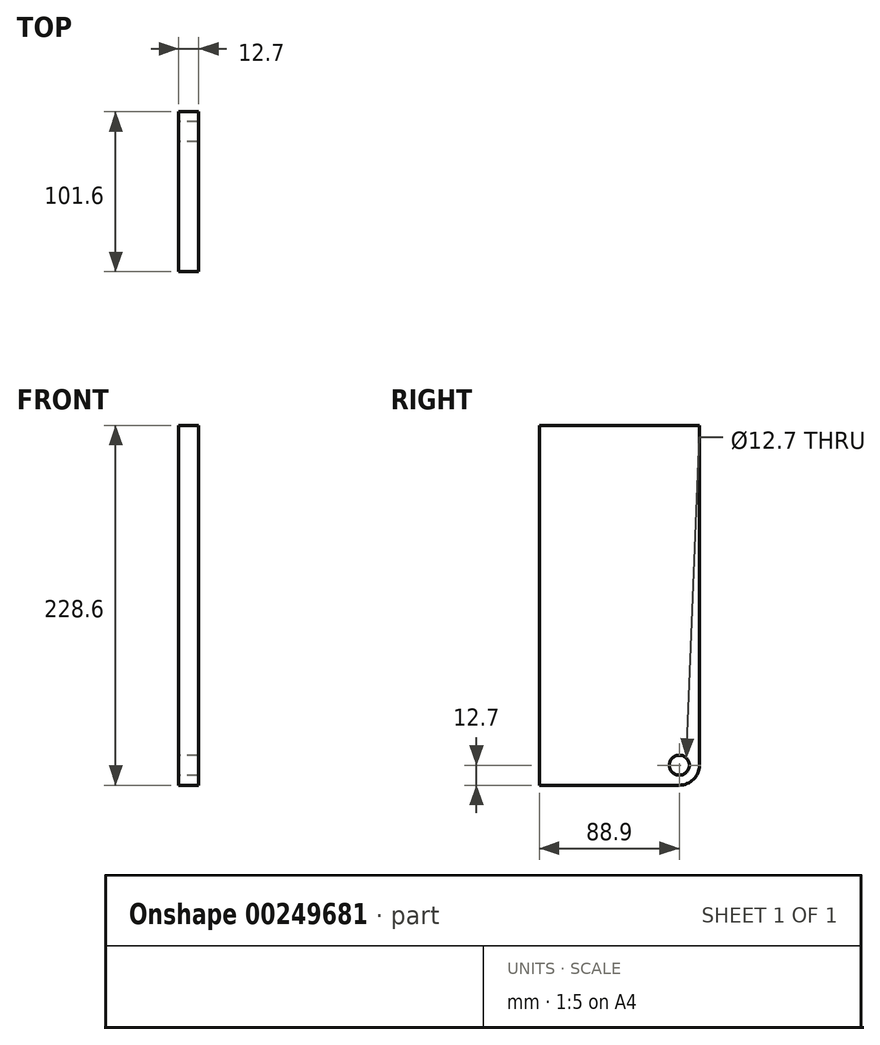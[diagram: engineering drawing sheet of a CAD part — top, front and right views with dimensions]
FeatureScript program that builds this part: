
annotation { "Feature Type Name" : "Feature", "Feature Type Description" : "" }
export const myFeature = defineFeature(function(context is Context, id is Id, definition is map)
    precondition{}
    {
        {
            var Q0;
            Q0=qCreatedBy(makeId("Right.planeOp"),FACE);
            var sketch = newSketch(context, id + "F0", { "sketchPlane" : qUnion([Q0])});
            skCircle(sketch, "E0", {"center": v(0, 0) * mm, "radius": 6.35 * mm});
            skArc(sketch, "E1", {"start": v(0, -12.7) * mm, "mid": v(8.98, -8.98) * mm, "end": v(12.7, 0) * mm});
            skLineSegment(sketch, "E2", {"start": v(12.7, 0) * mm, "end": v(12.7, 215.9) * mm});
            skLineSegment(sketch, "E3", {"start": v(12.7, 215.9) * mm, "end": v(-88.9, 215.9) * mm});
            skLineSegment(sketch, "E4", {"start": v(-88.9, 215.9) * mm, "end": v(-88.9, -12.7) * mm});
            skLineSegment(sketch, "E5", {"start": v(-88.9, -12.7) * mm, "end": v(0, -12.7) * mm});
            skSolve(sketch);
        }
        {
            var Q0;
            Q0 = qSketchRegion(id + "F0", true);
            extrude(context, id + "F1", {"entities" : qUnion([Q0]), "endBound" : BoundingType.SYMMETRIC, "depth" : 12.7 * mm});
        }
    });
